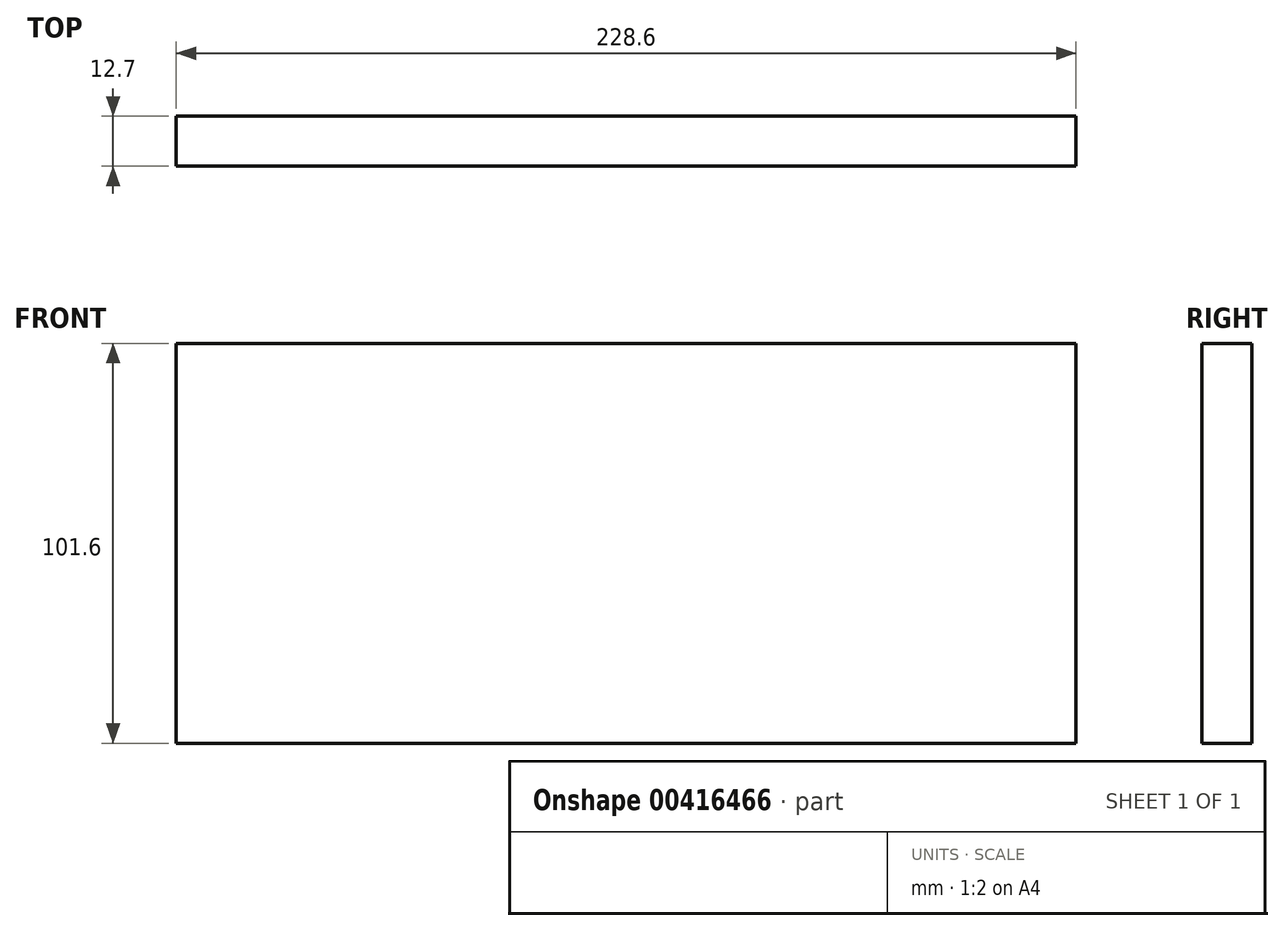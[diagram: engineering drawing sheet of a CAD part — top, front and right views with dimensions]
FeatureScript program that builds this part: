
annotation { "Feature Type Name" : "Feature", "Feature Type Description" : "" }
export const myFeature = defineFeature(function(context is Context, id is Id, definition is map)
    precondition{}
    {
        {
            var Q0;
            Q0=qCreatedBy(makeId("Front.planeOp"),FACE);
            var sketch = newSketch(context, id + "F0", { "sketchPlane" : qUnion([Q0])});
            skLineSegment(sketch, "E0", {"start": v(-107.85, 33.55) * mm, "end": v(120.75, 33.55) * mm});
            skLineSegment(sketch, "E1", {"start": v(120.75, 33.55) * mm, "end": v(120.75, -68.05) * mm});
            skLineSegment(sketch, "E2", {"start": v(120.75, -68.05) * mm, "end": v(-107.85, -68.05) * mm});
            skLineSegment(sketch, "E3", {"start": v(-107.85, -68.05) * mm, "end": v(-107.85, 33.55) * mm});
            skSolve(sketch);
        }
        {
            var Q0;
            Q0 = qSketchRegion(id + "F0", true);
            extrude(context, id + "F1", {"entities" : qUnion([Q0]), "depth" : 12.7 * mm});
        }
    });
